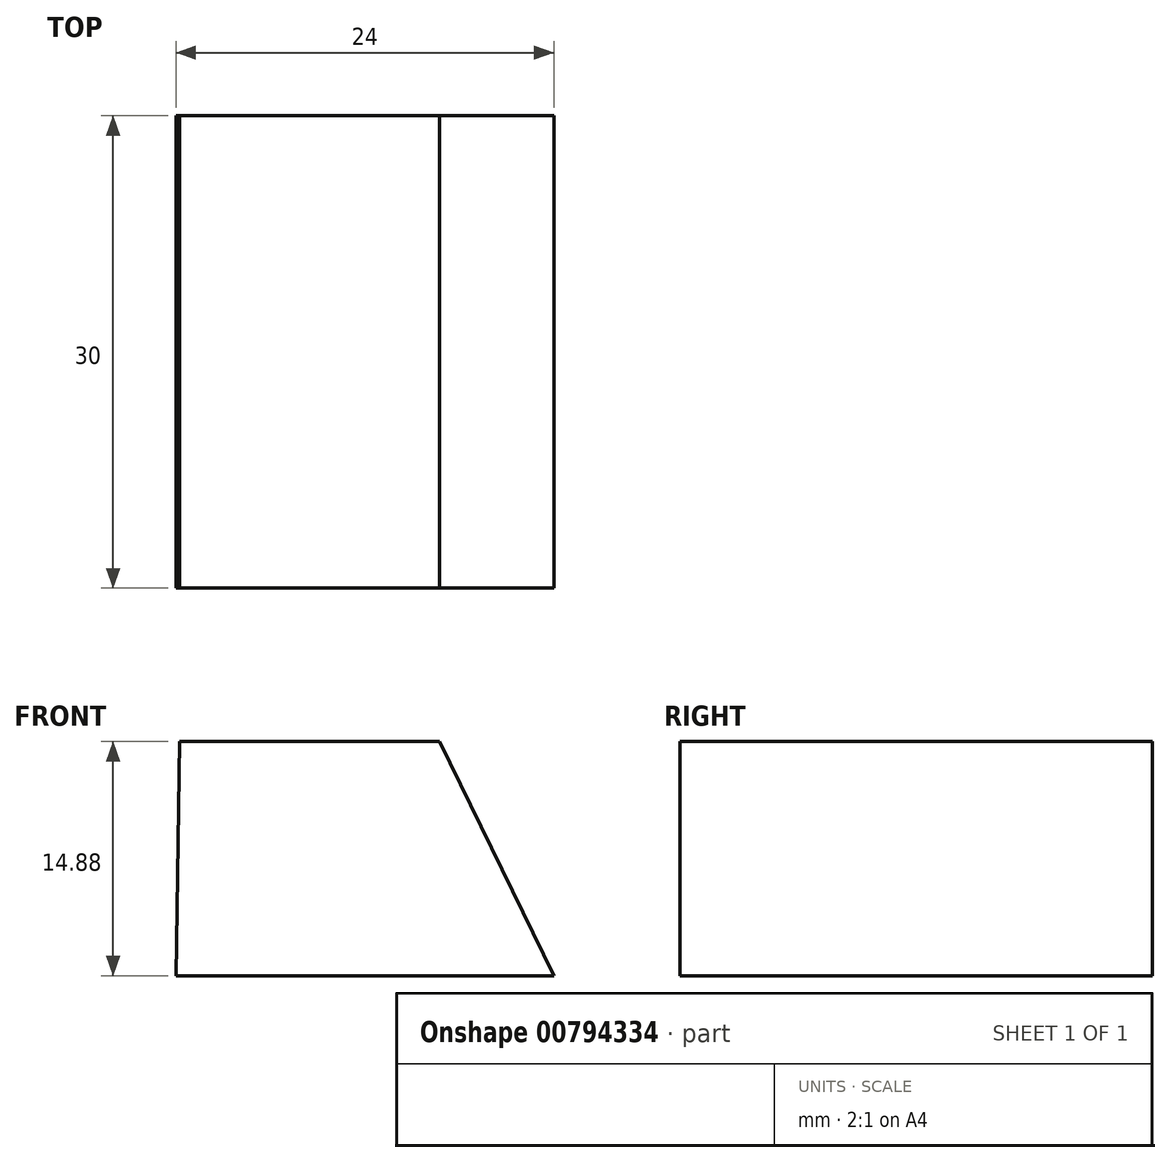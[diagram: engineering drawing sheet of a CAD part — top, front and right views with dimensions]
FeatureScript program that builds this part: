
annotation { "Feature Type Name" : "Feature", "Feature Type Description" : "" }
export const myFeature = defineFeature(function(context is Context, id is Id, definition is map)
    precondition{}
    {
        {
            var Q0;
            Q0=qCreatedBy(makeId("Front.planeOp"),FACE);
            var sketch = newSketch(context, id + "F0", { "sketchPlane" : qUnion([Q0])});
            skLineSegment(sketch, "E0", {"start": v(-9.05, 0.07) * mm, "end": v(14.95, 0.07) * mm});
            skLineSegment(sketch, "E1", {"start": v(14.95, 0.07) * mm, "end": v(7.68, 14.95) * mm});
            skLineSegment(sketch, "E2", {"start": v(7.68, 14.95) * mm, "end": v(-8.82, 14.95) * mm});
            skLineSegment(sketch, "E3", {"start": v(-8.82, 14.95) * mm, "end": v(-9.05, 0.07) * mm});
            skSolve(sketch);
        }
        {
            var Q0;
            Q0 = qSketchRegion(id + "F0", true);
            extrude(context, id + "F1", {"entities" : qUnion([Q0]), "depth" : 30 * mm, "offsetDistance" : 25 * mm});
        }
    });
